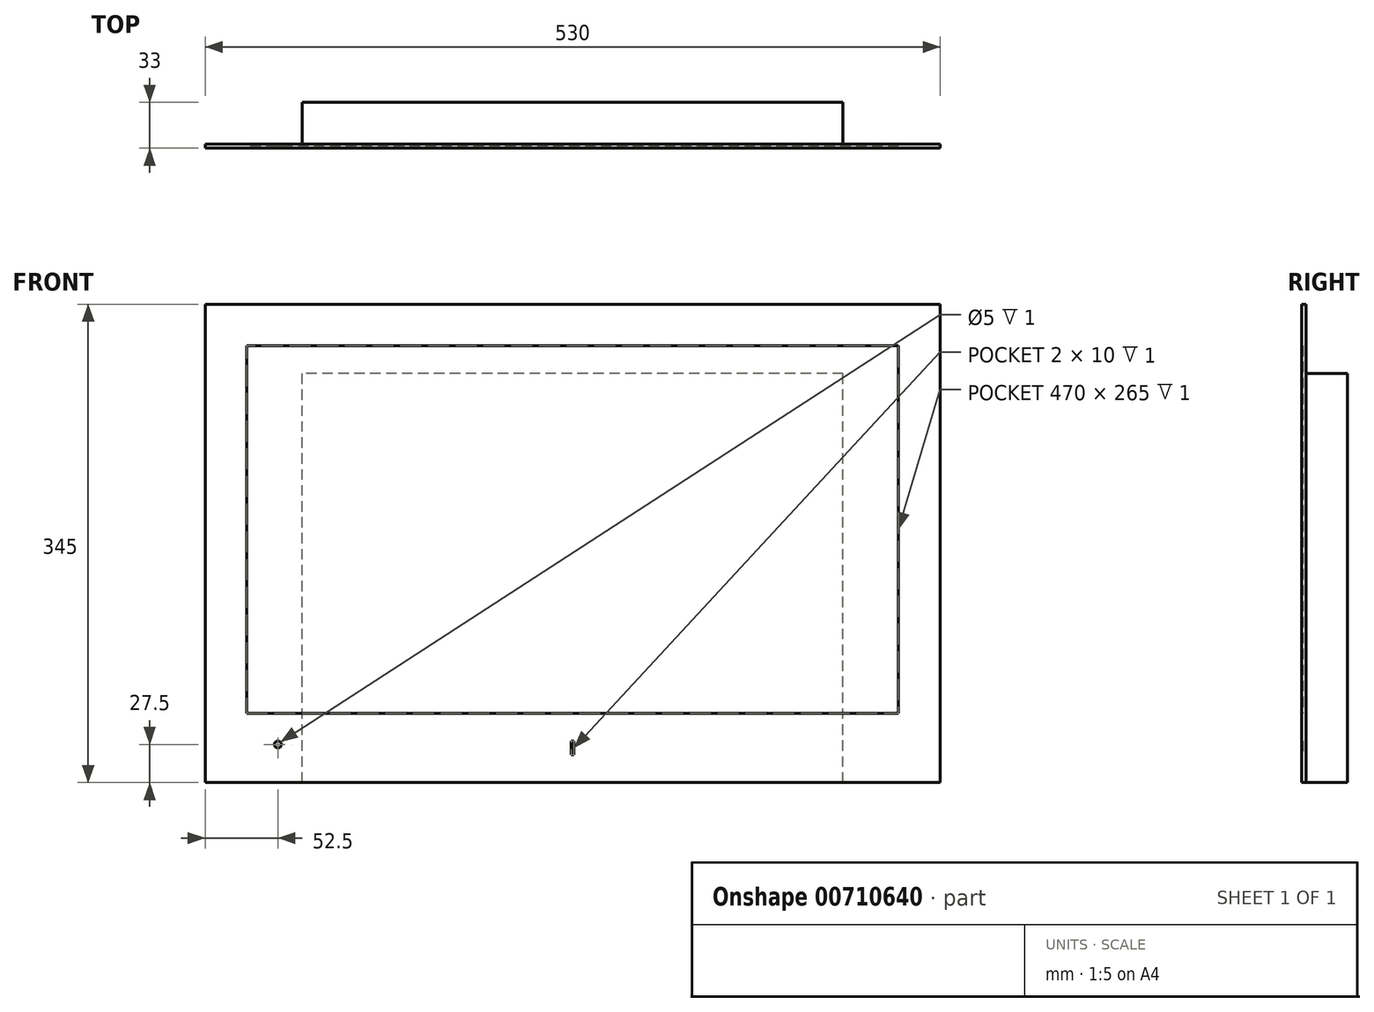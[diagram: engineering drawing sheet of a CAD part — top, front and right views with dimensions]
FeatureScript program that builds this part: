
annotation { "Feature Type Name" : "Feature", "Feature Type Description" : "" }
export const myFeature = defineFeature(function(context is Context, id is Id, definition is map)
    precondition{}
    {
        {
            var Q0;
            Q0=qCreatedBy(makeId("Front.planeOp"),FACE);
            var sketch = newSketch(context, id + "F0", { "sketchPlane" : qUnion([Q0])});
            skLineSegment(sketch, "E0.bottom", {"start": v(-265, 172.5) * mm, "end": v(265, 172.5) * mm});
            skLineSegment(sketch, "E0.top", {"start": v(-265, -172.5) * mm, "end": v(265, -172.5) * mm});
            skLineSegment(sketch, "E0.left", {"start": v(-265, 172.5) * mm, "end": v(-265, -172.5) * mm});
            skLineSegment(sketch, "E0.right", {"start": v(265, 172.5) * mm, "end": v(265, -172.5) * mm});
            skLineSegment(sketch, "E1.bottom", {"start": v(-235, 142.5) * mm, "end": v(235, 142.5) * mm});
            skLineSegment(sketch, "E1.top", {"start": v(-235, -122.5) * mm, "end": v(235, -122.5) * mm});
            skLineSegment(sketch, "E1.left", {"start": v(-235, 142.5) * mm, "end": v(-235, -122.5) * mm});
            skLineSegment(sketch, "E1.right", {"start": v(235, 142.5) * mm, "end": v(235, -122.5) * mm});
            skCircle(sketch, "E2", {"center": v(-212.5, -145) * mm, "radius": 2.5 * mm});
            skLineSegment(sketch, "E3.bottom", {"start": v(-1, -142.5) * mm, "end": v(1, -142.5) * mm});
            skLineSegment(sketch, "E3.top", {"start": v(-1, -152.5) * mm, "end": v(1, -152.5) * mm});
            skLineSegment(sketch, "E3.left", {"start": v(-1, -142.5) * mm, "end": v(-1, -152.5) * mm});
            skLineSegment(sketch, "E3.right", {"start": v(1, -142.5) * mm, "end": v(1, -152.5) * mm});
            skSolve(sketch);
        }
        {
            var Q0;
            Q0=makeQuery(id+"F0.imprint","IMPRINT",FACE,{"disambiguationData":[TD([[makeQuery(id+"F0.imprint","IMPRINT",EDGE,{"derivedFrom":sQuery(id+"F0.wireOp",EDGE,"E1.bottom")}),-1.0]])]});
            var Q1;
            Q1=makeQuery(id+"F0.imprint","IMPRINT",FACE,{"disambiguationData":[TD([[makeQuery(id+"F0.imprint","IMPRINT",EDGE,{"derivedFrom":sQuery(id+"F0.wireOp",EDGE,"E0.bottom")}),-1.0]])]});
            var Q2;
            Q2=makeQuery(id+"F0.imprint","IMPRINT",FACE,{"disambiguationData":[TD([[makeQuery(id+"F0.imprint","IMPRINT",EDGE,{"derivedFrom":sQuery(id+"F0.wireOp",EDGE,"E2")}),1.0]])]});
            var Q3;
            Q3=makeQuery(id+"F0.imprint","IMPRINT",FACE,{"disambiguationData":[TD([[makeQuery(id+"F0.imprint","IMPRINT",EDGE,{"derivedFrom":sQuery(id+"F0.wireOp",EDGE,"E3.bottom")}),-1.0]])]});
            extrude(context, id + "F1", {"entities" : qUnion([Q0, Q1, Q2, Q3]), "depth" : 3 * mm, "offsetDistance" : 25 * mm});
        }
        {
            var Q0;
            Q0=makeQuery(id+"F1.opExtrude","CAP_FACE",FACE,{"disambiguationData":[OSD([sQuery(id+"F0.wireOp",EDGE,"E0.bottom"),sQuery(id+"F0.wireOp",EDGE,"E0.top"),sQuery(id+"F0.wireOp",EDGE,"E0.left"),sQuery(id+"F0.wireOp",EDGE,"E0.right")])],"isStart":false});
            var sketch = newSketch(context, id + "F2", { "sketchPlane" : qUnion([Q0])});
            skLineSegment(sketch, "E4.bottom", {"start": v(235, 142.5) * mm, "end": v(-235, 142.5) * mm});
            skLineSegment(sketch, "E4.top", {"start": v(235, -122.5) * mm, "end": v(-235, -122.5) * mm});
            skLineSegment(sketch, "E4.left", {"start": v(235, 142.5) * mm, "end": v(235, -122.5) * mm});
            skLineSegment(sketch, "E4.right", {"start": v(-235, 142.5) * mm, "end": v(-235, -122.5) * mm});
            skCircle(sketch, "E5", {"center": v(-212.5, -145) * mm, "radius": 2.5 * mm});
            skLineSegment(sketch, "E6.bottom", {"start": v(1, -142.5) * mm, "end": v(-1, -142.5) * mm});
            skLineSegment(sketch, "E6.top", {"start": v(1, -152.5) * mm, "end": v(-1, -152.5) * mm});
            skLineSegment(sketch, "E6.left", {"start": v(1, -142.5) * mm, "end": v(1, -152.5) * mm});
            skLineSegment(sketch, "E6.right", {"start": v(-1, -142.5) * mm, "end": v(-1, -152.5) * mm});
            skSolve(sketch);
        }
        {
            var Q0;
            Q0 = qSketchRegion(id + "F2", true);
            extrude(context, id + "F3", {"entities" : qUnion([Q0]), "operationType" : NewBodyOperationType.REMOVE, "oppositeDirection" : true, "depth" : 1 * mm, "offsetDistance" : 25 * mm});
        }
        {
            var Q0;
            Q0=makeQuery(id+"F0.imprint","IMPRINT",FACE,{"disambiguationData":[TD([[makeQuery(id+"F0.imprint","IMPRINT",EDGE,{"derivedFrom":sQuery(id+"F0.wireOp",EDGE,"E0.bottom")}),-1.0]])]});
            var sketch = newSketch(context, id + "F4", { "sketchPlane" : qUnion([Q0])});
            skLineSegment(sketch, "E7.bottom", {"start": v(195, -172.5) * mm, "end": v(-195, -172.5) * mm});
            skLineSegment(sketch, "E7.top", {"start": v(195, 122.5) * mm, "end": v(-195, 122.5) * mm});
            skLineSegment(sketch, "E7.left", {"start": v(195, -172.5) * mm, "end": v(195, 122.5) * mm});
            skLineSegment(sketch, "E7.right", {"start": v(-195, -172.5) * mm, "end": v(-195, 122.5) * mm});
            skSolve(sketch);
        }
        {
            var Q0;
            Q0 = qSketchRegion(id + "F4", true);
            var Q1;
            {var subQ0=sQuery(id+"F4.wireOp",EDGE,"E7.top");Q1=makeQuery(id+"F4.imprint","IMPRINT",FACE,{"disambiguationData":[TD([[makeQuery(id+"F4.imprint","IMPRINT",EDGE,{"derivedFrom":subQ0}),1.0]])]});}
            extrude(context, id + "F5", {"entities" : qUnion([Q0, Q1]), "operationType" : NewBodyOperationType.ADD, "depth" : -30 * mm, "offsetDistance" : 25 * mm});
        }
    });
